# Revit family: hb_304_612109_002_a26b
name_source: partatom
category: Lighting Fixtures
units: mm (PartAtom-declared; Revit-internal decimal feet)

## family parameters
Cut with Voids When Loaded = No
Host = Face
Light Source = No
Part Type = Normal
Room Calculation Point = No
Round Connector Dimension = Use Diameter
Shared = No

## types (1)
- HB 304 (1 x LED Modul RGBW, 400 lm, 2800)
    Apparent Load = 9 VA
    CIE Flux Codes = 14 28 50 8 100
    Color Rendering = 80
    Color Temperature = 2800
    Default Elevation = 1800 mm
    Description = Series: HB 304
Decorative garden luminaire. Sphere can float in water and feature a flat base. Plastic base with opal plastic (polyethylene) diffuser sphere, satin finish. LED with colour change sequencer for battery operation - tuneable coloured light RGB or white. Light control via IR remote control. Full charge service life 8 to 12 hours (continuous operation). External charger for 100 - 240 V / 50 - 60 Hz with an inductive cradle included. Charge in dry rooms only! 
Colour: white
Diameter: 500 mm
Height: 500 mm
Lamp: LED
System power: 9 W
Rated luminous flux: 400 lm
Luminous efficiency: 44 lm/W
Control gear: Converter, dimmable, infra-red
Protection class: II
Type of protection: IP 68
    Height = 500 mm
    Lamp = 1 x LED Modul RGBW
    Lamp Light Flux = 400 lm
    Lamp count = 1
    Length = 500 mm
    Lifetime = 50000 h
    Luminous efficacy = 44 lm/W
    Manufacturer = RZB
    ModVariant = No
    Model = 612109.002
    Mounting Place = Floor
    Mounting Type = Freestanding
    Number of Poles = 1
    OnlyDefault = Yes
    Power Factor = 1
    Product Name = HB 304
    Product group = Stehleuchten
    ProductGroupID = 1355
    Protection Class = Protection class II
    Protection Degree = IP 68
    RLX_Detail_Level = 1
    RLX_Emergency_Light_Flux = 0 lm
    RLX_Emergency_Type = 0
    RLX_Emergency_Type_DB = No
    RlxData = <blob elided: 167197 chars, md5=e7de1b70>
    Socket = socket
    Standby Power = 0 W
    System Light Flux = 400 lm
    System Power = 9 W
    Type Comments = Product without accessories
    Type Image = 612109.002.jpg
    URL = http://relux.com
    VarID = ---
    Voltage = 0 V
    Weight = 0.00 kg
    Width = 0 mm  [stored 0 ft]

note: [stored X ft] marks values corroborated as IEEE doubles in the binary element streams (Revit-internal decimal feet)

## geometry (parser evidence)
native form markers: Blend x4, Sweep x13
no freeform markers — native parametric forms only
